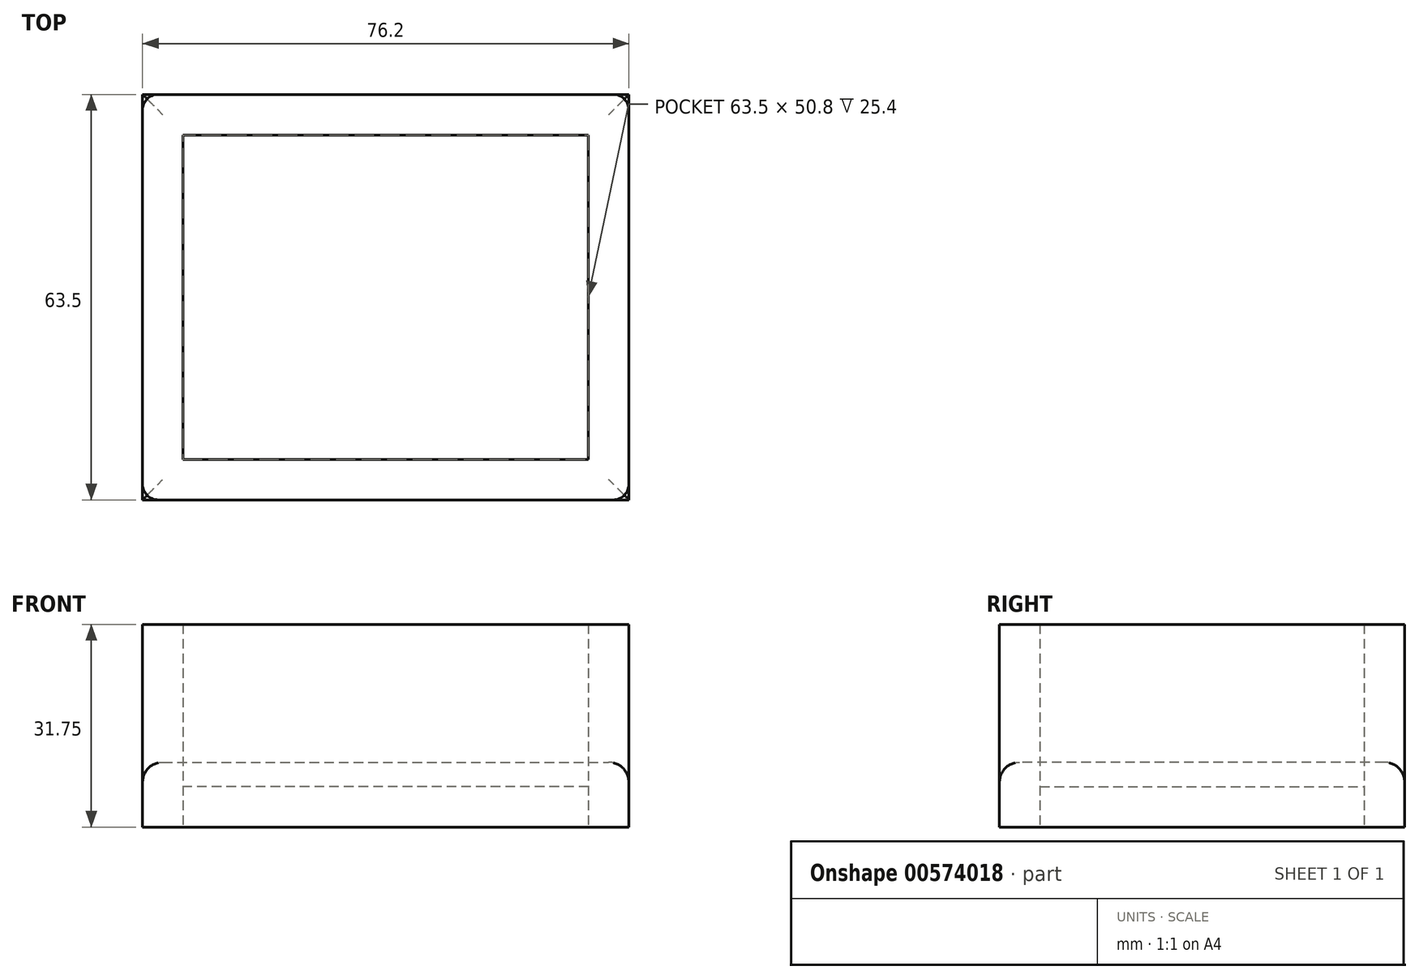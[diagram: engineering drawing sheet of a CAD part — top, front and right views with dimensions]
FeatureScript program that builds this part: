
annotation { "Feature Type Name" : "Feature", "Feature Type Description" : "" }
export const myFeature = defineFeature(function(context is Context, id is Id, definition is map)
    precondition{}
    {
        {
            var Q0;
            Q0=qCreatedBy(makeId("Top.planeOp"),FACE);
            var sketch = newSketch(context, id + "F0", { "sketchPlane" : qUnion([Q0])});
            skLineSegment(sketch, "E0.bottom", {"start": v(-38.1, 31.75) * mm, "end": v(38.1, 31.75) * mm});
            skLineSegment(sketch, "E0.top", {"start": v(-38.1, -31.75) * mm, "end": v(38.1, -31.75) * mm});
            skLineSegment(sketch, "E0.left", {"start": v(-38.1, 31.75) * mm, "end": v(-38.1, -31.75) * mm});
            skLineSegment(sketch, "E0.right", {"start": v(38.1, 31.75) * mm, "end": v(38.1, -31.75) * mm});
            skPoint(sketch, "E0.middle", {"position": v(0, 0) * mm});
            skLineSegment(sketch, "E1.bottom", {"start": v(31.75, -25.4) * mm, "end": v(-31.75, -25.4) * mm});
            skLineSegment(sketch, "E1.top", {"start": v(31.75, 25.4) * mm, "end": v(-31.75, 25.4) * mm});
            skLineSegment(sketch, "E1.left", {"start": v(31.75, -25.4) * mm, "end": v(31.75, 25.4) * mm});
            skLineSegment(sketch, "E1.right", {"start": v(-31.75, -25.4) * mm, "end": v(-31.75, 25.4) * mm});
            skSolve(sketch);
        }
        {
            var Q0;
            Q0=makeQuery(id+"F0.imprint","IMPRINT",FACE,{"disambiguationData":[TD([[makeQuery(id+"F0.imprint","IMPRINT",EDGE,{"derivedFrom":sQuery(id+"F0.wireOp",EDGE,"E0.bottom")}),-1.0]])]});
            extrude(context, id + "F1", {"entities" : qUnion([Q0]), "depth" : 31.75 * mm, "offsetDistance" : 25.4 * mm});
        }
        {
            var Q0;
            Q0=makeQuery(id+"F0.imprint","IMPRINT",FACE,{"disambiguationData":[TD([[makeQuery(id+"F0.imprint","IMPRINT",EDGE,{"derivedFrom":sQuery(id+"F0.wireOp",EDGE,"E1.bottom")}),-1.0]])]});
            extrude(context, id + "F2", {"entities" : qUnion([Q0]), "operationType" : NewBodyOperationType.ADD, "depth" : 6.35 * mm, "offsetDistance" : 25.4 * mm});
        }
        {
            var Q0;
            Q0=makeQuery(id+"F1.opExtrude","SWEPT_EDGE",EDGE,{"disambiguationData":[OSD([sQuery(id+"F0.wireOp",EDGE,"E0.bottom"),sQuery(id+"F0.wireOp",EDGE,"E0.left")])]});
            var Q1;
            Q1=makeQuery(id+"F1.opExtrude","SWEPT_EDGE",EDGE,{"disambiguationData":[OSD([sQuery(id+"F0.wireOp",EDGE,"E0.bottom"),sQuery(id+"F0.wireOp",EDGE,"E0.right")])]});
            var Q2;
            Q2=makeQuery(id+"F1.opExtrude","SWEPT_EDGE",EDGE,{"disambiguationData":[OSD([sQuery(id+"F0.wireOp",EDGE,"E0.top"),sQuery(id+"F0.wireOp",EDGE,"E0.right")])]});
            var Q3;
            Q3=makeQuery(id+"F1.opExtrude","SWEPT_EDGE",EDGE,{"disambiguationData":[OSD([sQuery(id+"F0.wireOp",EDGE,"E0.top"),sQuery(id+"F0.wireOp",EDGE,"E0.left")])]});
            fillet(context, id + "F3", {"entities" : qUnion([Q0, Q1, Q2, Q3]), "radius" : 2.45 * mm, "tangentPropagation" : true, "allowEdgeOverflow" : false});
        }
        {
            var Q0;
            Q0=makeQuery(id+"F0.imprint","IMPRINT",FACE,{"disambiguationData":[TD([[makeQuery(id+"F0.imprint","IMPRINT",EDGE,{"derivedFrom":sQuery(id+"F0.wireOp",EDGE,"E0.bottom")}),-1.0]])]});
            var Q1;
            Q1=makeQuery(id+"F0.imprint","IMPRINT",FACE,{"disambiguationData":[TD([[makeQuery(id+"F0.imprint","IMPRINT",EDGE,{"derivedFrom":sQuery(id+"F0.wireOp",EDGE,"E1.bottom")}),-1.0]])]});
            extrude(context, id + "F4", {"entities" : qUnion([Q0, Q1]), "depth" : 10.16 * mm, "offsetDistance" : 25.4 * mm});
        }
        {
            var Q0;
            Q0=makeQuery(id+"F4.opExtrude","CAP_EDGE",EDGE,{"disambiguationData":[OSD([sQuery(id+"F0.wireOp",EDGE,"E0.top")])],"isStart":false});
            var Q1;
            Q1=makeQuery(id+"F4.opExtrude","CAP_EDGE",EDGE,{"disambiguationData":[OSD([sQuery(id+"F0.wireOp",EDGE,"E0.left")])],"isStart":false});
            var Q2;
            Q2=makeQuery(id+"F4.opExtrude","CAP_EDGE",EDGE,{"disambiguationData":[OSD([sQuery(id+"F0.wireOp",EDGE,"E0.right")])],"isStart":false});
            var Q3;
            Q3=makeQuery(id+"F4.opExtrude","CAP_EDGE",EDGE,{"disambiguationData":[OSD([sQuery(id+"F0.wireOp",EDGE,"E0.bottom")])],"isStart":false});
            fillet(context, id + "F5", {"entities" : qUnion([Q0, Q1, Q2, Q3]), "radius" : 3.17 * mm, "tangentPropagation" : true, "allowEdgeOverflow" : false});
        }
        {
            var Q0;
            Q0=makeQuery(id+"F0.imprint","IMPRINT",FACE,{"disambiguationData":[TD([[makeQuery(id+"F0.imprint","IMPRINT",EDGE,{"derivedFrom":sQuery(id+"F0.wireOp",EDGE,"E1.bottom")}),-1.0]])]});
            extrude(context, id + "F6", {"entities" : qUnion([Q0]), "depth" : 31.75 * mm, "offsetDistance" : 25.4 * mm});
        }
    });
